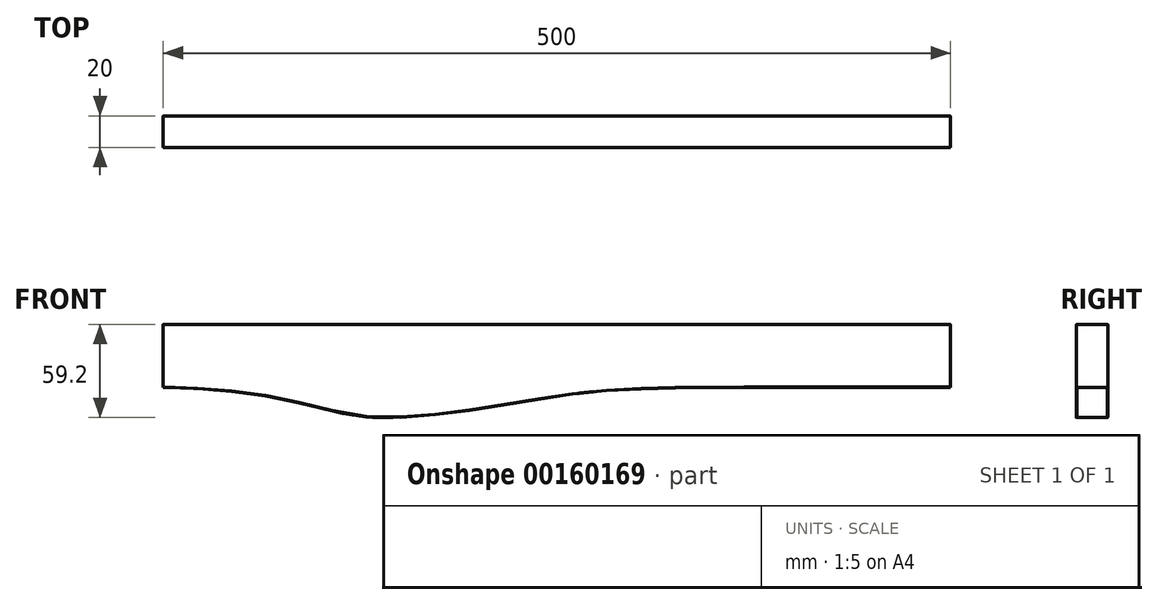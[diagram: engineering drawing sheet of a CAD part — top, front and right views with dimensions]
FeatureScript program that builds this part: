
annotation { "Feature Type Name" : "Feature", "Feature Type Description" : "" }
export const myFeature = defineFeature(function(context is Context, id is Id, definition is map)
    precondition{}
    {
        {
            var Q0;
            Q0=qCreatedBy(makeId("Front.planeOp"),FACE);
            var sketch = newSketch(context, id + "F0", { "sketchPlane" : qUnion([Q0])});
            skLineSegment(sketch, "E0.bottom", {"start": v(-561.83, 90.47) * mm, "end": v(-61.83, 90.47) * mm});
            skLineSegment(sketch, "E0.left", {"start": v(-561.83, 90.47) * mm, "end": v(-561.83, 50.47) * mm});
            skLineSegment(sketch, "E0.right", {"start": v(-61.83, 90.47) * mm, "end": v(-61.83, 50.47) * mm});
            skFitSpline(sketch, "E1", {"points": [v(-561.83, 50.47) * mm, v(-429.28, 31.54) * mm, v(-320.03, 43.55) * mm, v(-61.83, 50.47) * mm], "startDerivative": vector(811.71, -15.5) * mm, "endDerivative": vector(1392.6, 0.37) * mm});
            skSolve(sketch);
        }
        {
            var Q0;
            Q0=makeQuery(id+"F0.imprint","IMPRINT",FACE,{"disambiguationData":[TD([[makeQuery(id+"F0.imprint","IMPRINT",EDGE,{"derivedFrom":sQuery(id+"F0.wireOp",EDGE,"E0.bottom")}),-1.0]])]});
            var Q1;
            Q1 = qSketchRegion(id + "F0", true);
            extrude(context, id + "F1", {"entities" : qUnion([Q0, Q1]), "depth" : 20 * mm});
        }
        {
            var Q0;
            Q0=makeQuery(id+"F1.opExtrude","CAP_FACE",FACE,{"disambiguationData":[OSD([sQuery(id+"F0.wireOp",EDGE,"E0.bottom"),sQuery(id+"F0.wireOp",EDGE,"E0.left"),sQuery(id+"F0.wireOp",EDGE,"E0.right"),sQuery(id+"F0.wireOp",EDGE,"E1")])],"isStart":false});
            var Q1;
            Q1=makeQuery(id+"F1.opExtrude","CAP_FACE",FACE,{"disambiguationData":[OSD([sQuery(id+"F0.wireOp",EDGE,"E0.bottom"),sQuery(id+"F0.wireOp",EDGE,"E0.left"),sQuery(id+"F0.wireOp",EDGE,"E0.right"),sQuery(id+"F0.wireOp",EDGE,"E1")])],"isStart":true});
            fillet(context, id + "F2", {"entities" : qUnion([Q0, Q1]), "radius" : 0.2 * mm, "tangentPropagation" : true, "allowEdgeOverflow" : false});
        }
    });
